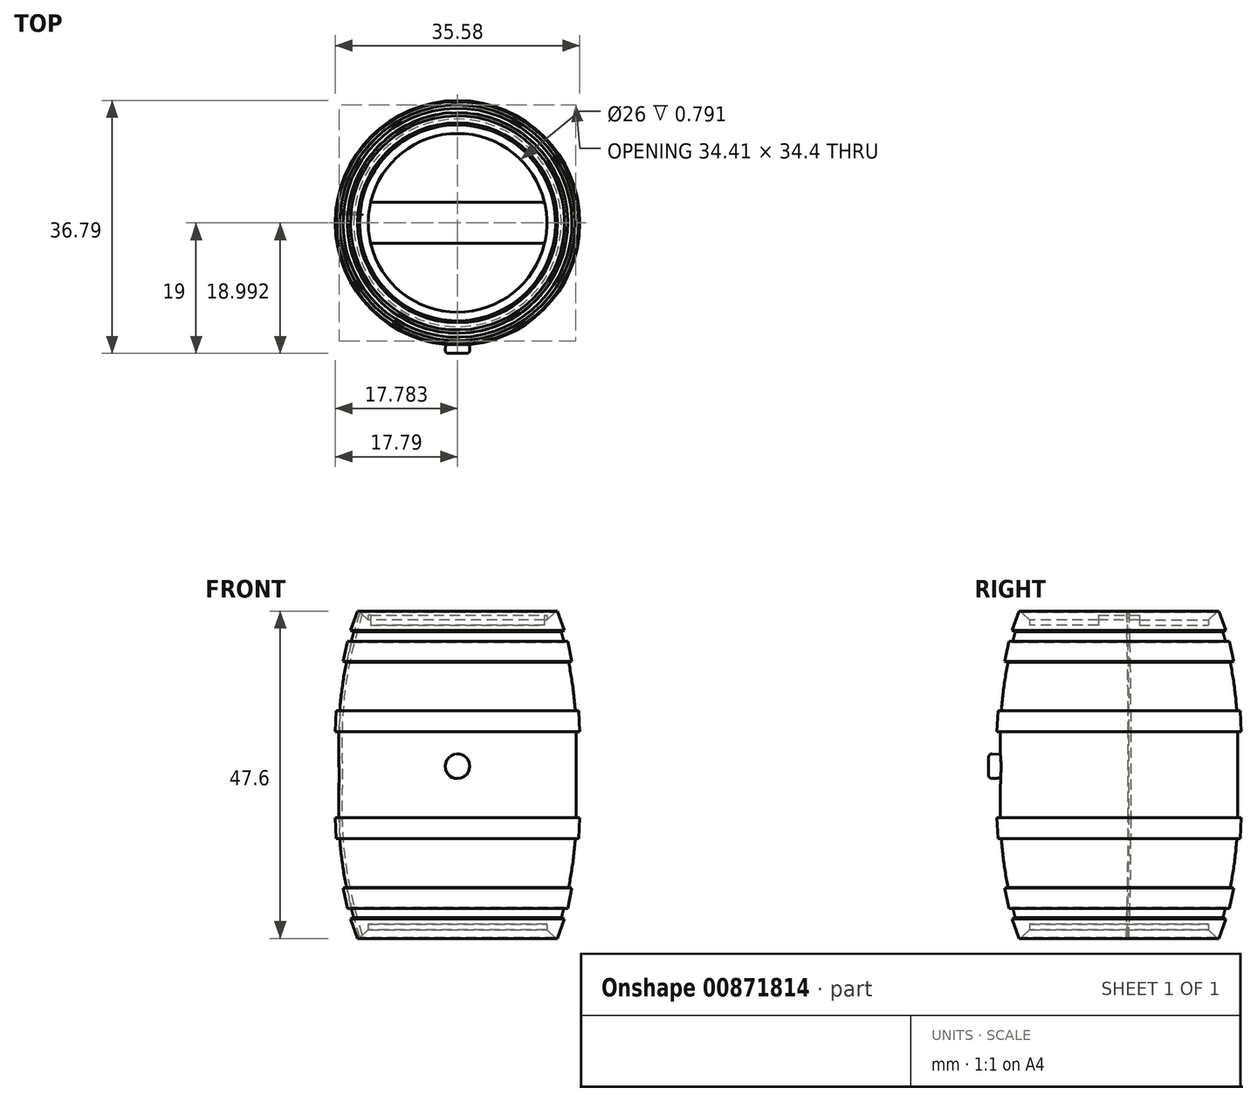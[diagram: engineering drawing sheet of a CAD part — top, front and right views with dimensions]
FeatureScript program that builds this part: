
annotation { "Feature Type Name" : "Feature", "Feature Type Description" : "" }
export const myFeature = defineFeature(function(context is Context, id is Id, definition is map)
    precondition{}
    {
        {
            var Q0;
            Q0=qCreatedBy(makeId("Front.planeOp"),FACE);
            var sketch = newSketch(context, id + "F0", { "sketchPlane" : qUnion([Q0])});
            skLineSegment(sketch, "E0.left", {"start": v(0, 2) * mm, "end": v(0, 45.5) * mm});
            skLineSegment(sketch, "E0.right", {"start": v(-14.25, 0.06) * mm, "end": v(-14.25, 47.44) * mm, "construction": true});
            skPoint(sketch, "E1.positionSnap0", {"position": v(-14.25, 23.75) * mm});
            skFitSpline(sketch, "E2", {"points": [v(-14.25, 0.06) * mm, v(-17.25, 23.75) * mm, v(-14.25, 47.44) * mm], "startDerivative": vector(-21.33, 67.5) * mm, "endDerivative": vector(21.33, 67.5) * mm});
            skLineSegment(sketch, "E3", {"start": v(-13, 45.5) * mm, "end": v(0, 45.5) * mm});
            skLineSegment(sketch, "E4", {"start": v(-13, 45.5) * mm, "end": v(-13, 46.3) * mm});
            skLineSegment(sketch, "E5", {"start": v(-13, 46.3) * mm, "end": v(-14.25, 47.44) * mm});
            skLineSegment(sketch, "E6", {"start": v(6.25, 23.75) * mm, "end": v(9.53, 23.75) * mm, "construction": true});
            skPoint(sketch, "E6.startSnap0", {"position": v(0, 23.75) * mm});
            skLineSegment(sketch, "E7", {"start": v(-14.25, 47.44) * mm, "end": v(-14.55, 47.55) * mm});
            skLineSegment(sketch, "E8", {"start": v(-14.55, 47.55) * mm, "end": v(-15.57, 44.73) * mm});
            skLineSegment(sketch, "E9", {"start": v(-15.57, 44.73) * mm, "end": v(-15.1, 44.56) * mm});
            skLineSegment(sketch, "E10", {"start": v(-15.5, 43.06) * mm, "end": v(-16.03, 43.17) * mm});
            skLineSegment(sketch, "E11", {"start": v(-16.03, 43.17) * mm, "end": v(-16.65, 40.23) * mm});
            skLineSegment(sketch, "E12", {"start": v(-16.65, 40.23) * mm, "end": v(-16.17, 40.13) * mm});
            skPoint(sketch, "E13.orphan", {"position": v(0, 47.5) * mm});
            skLineSegment(sketch, "E14", {"start": v(-17.14, 33) * mm, "end": v(-17.63, 33.04) * mm});
            skLineSegment(sketch, "E15", {"start": v(-17.63, 33.04) * mm, "end": v(-17.8, 30) * mm});
            skLineSegment(sketch, "E16", {"start": v(-17.8, 30) * mm, "end": v(-17.27, 30) * mm});
            skLineSegment(sketch, "E17.MirrorCS", {"start": v(-14.25, 0.06) * mm, "end": v(-14.55, -0.05) * mm});
            skLineSegment(sketch, "E18.MirrorCS", {"start": v(-15.57, 2.77) * mm, "end": v(-15.1, 2.94) * mm});
            skLineSegment(sketch, "E19.MirrorCS", {"start": v(-17.8, 17.5) * mm, "end": v(-17.27, 17.5) * mm});
            skLineSegment(sketch, "E20.MirrorCS", {"start": v(-16.65, 7.27) * mm, "end": v(-16.17, 7.37) * mm});
            skLineSegment(sketch, "E21.MirrorCS", {"start": v(-17.14, 14.5) * mm, "end": v(-17.63, 14.46) * mm});
            skLineSegment(sketch, "E22.MirrorCS", {"start": v(-15.5, 4.44) * mm, "end": v(-16.03, 4.33) * mm});
            skLineSegment(sketch, "E23.MirrorCS", {"start": v(-17.63, 14.46) * mm, "end": v(-17.8, 17.5) * mm});
            skLineSegment(sketch, "E24.MirrorCS", {"start": v(-14.55, -0.05) * mm, "end": v(-15.57, 2.77) * mm});
            skLineSegment(sketch, "E25.MirrorCS", {"start": v(-16.03, 4.33) * mm, "end": v(-16.65, 7.27) * mm});
            skLineSegment(sketch, "E26.MirrorCS", {"start": v(-13, 2) * mm, "end": v(0, 2) * mm});
            skLineSegment(sketch, "E27.MirrorCS", {"start": v(-13, 2) * mm, "end": v(-13, 1.2) * mm});
            skLineSegment(sketch, "E28.MirrorCS", {"start": v(-13, 1.2) * mm, "end": v(-14.25, 0.06) * mm});
            skPoint(sketch, "E29.orphan", {"position": v(0, 0) * mm});
            skSolve(sketch);
        }
        {
            var Q0;
            Q0=makeQuery(id+"F0.imprint","IMPRINT",FACE,{"disambiguationData":[TD([[makeQuery(id+"F0.imprint","IMPRINT",EDGE,{"derivedFrom":sQuery(id+"F0.wireOp",EDGE,"E0.left")}),1.0]])]});
            var Q1;
            Q1=sQuery(id+"F0.wireOp",EDGE,"E0.left");
            revolve(context, id + "F1", {"surfaceOperationType" : NewSurfaceOperationType.NEW, "entities" : qUnion([Q0]), "axis" : qUnion([Q1]), "revolveType" : RevolveType.FULL});
        }
        {
            var Q0;
            Q0=qCreatedBy(makeId("Top.planeOp"),FACE);
            var sketch = newSketch(context, id + "F2", { "sketchPlane" : qUnion([Q0])});
            skLineSegment(sketch, "E30", {"start": v(-13.75, 0) * mm, "end": v(6.9, 0) * mm, "construction": true});
            skLineSegment(sketch, "E31", {"start": v(-14.35, 0.22) * mm, "end": v(-13.75, 0) * mm});
            skLineSegment(sketch, "E32", {"start": v(-14.35, -0.22) * mm, "end": v(-14.35, 0.22) * mm});
            skLineSegment(sketch, "E33", {"start": v(-13.75, 0) * mm, "end": v(-14.35, -0.22) * mm});
            skSolve(sketch);
        }
        {
            var Q0;
            Q0=makeQuery(id+"F2.imprint","IMPRINT",FACE,{"disambiguationData":[TD([[makeQuery(id+"F2.imprint","IMPRINT",EDGE,{"derivedFrom":sQuery(id+"F2.wireOp",EDGE,"E31")}),-1.0]])]});
            var Q1;
            Q1=sQuery(id+"F0.wireOp",EDGE,"E2");
            sweep(context, id + "F3", {"operationType" : NewBodyOperationType.REMOVE, "profiles" : qUnion([Q0]), "path" : qUnion([Q1])});
        }
        {
            var Q0;
            {var subQ0=sQuery(id+"F0.wireOp",EDGE,"E7");Q0=makeQuery(id+"F0.imprint","IMPRINT",FACE,{"disambiguationData":[TD([[makeQuery(id+"F0.imprint","IMPRINT",EDGE,{"derivedFrom":subQ0}),1.0]])]});}
            var Q1;
            {var subQ0=sQuery(id+"F0.wireOp",EDGE,"E10");Q1=makeQuery(id+"F0.imprint","IMPRINT",FACE,{"disambiguationData":[TD([[makeQuery(id+"F0.imprint","IMPRINT",EDGE,{"derivedFrom":subQ0}),1.0]])]});}
            var Q2;
            {var subQ0=sQuery(id+"F0.wireOp",EDGE,"E14");Q2=makeQuery(id+"F0.imprint","IMPRINT",FACE,{"disambiguationData":[TD([[makeQuery(id+"F0.imprint","IMPRINT",EDGE,{"derivedFrom":subQ0}),1.0]])]});}
            var Q3;
            {var subQ0=sQuery(id+"F0.wireOp",EDGE,"E19.MirrorCS");Q3=makeQuery(id+"F0.imprint","IMPRINT",FACE,{"disambiguationData":[TD([[makeQuery(id+"F0.imprint","IMPRINT",EDGE,{"derivedFrom":subQ0}),-1.0]])]});}
            var Q4;
            {var subQ0=sQuery(id+"F0.wireOp",EDGE,"E20.MirrorCS");Q4=makeQuery(id+"F0.imprint","IMPRINT",FACE,{"disambiguationData":[TD([[makeQuery(id+"F0.imprint","IMPRINT",EDGE,{"derivedFrom":subQ0}),-1.0]])]});}
            var Q5;
            {var subQ0=sQuery(id+"F0.wireOp",EDGE,"E17.MirrorCS");Q5=makeQuery(id+"F0.imprint","IMPRINT",FACE,{"disambiguationData":[TD([[makeQuery(id+"F0.imprint","IMPRINT",EDGE,{"derivedFrom":subQ0}),-1.0]])]});}
            var Q6;
            Q6=sQuery(id+"F0.wireOp",EDGE,"E0.left");
            revolve(context, id + "F4", {"operationType" : NewBodyOperationType.ADD, "surfaceOperationType" : NewSurfaceOperationType.NEW, "entities" : qUnion([Q0, Q1, Q2, Q3, Q4, Q5]), "axis" : qUnion([Q6]), "revolveType" : RevolveType.FULL});
        }
        {
            var Q0;
            Q0=makeQuery(id+"F1.opRevolve","SWEPT_BODY",BODY,{"disambiguationData":[OSD([sQuery(id+"F0.wireOp",EDGE,"E0.left"),sQuery(id+"F0.wireOp",EDGE,"E2"),sQuery(id+"F0.wireOp",EDGE,"E3"),sQuery(id+"F0.wireOp",EDGE,"E4"),sQuery(id+"F0.wireOp",EDGE,"E5"),sQuery(id+"F0.wireOp",EDGE,"E26.MirrorCS"),sQuery(id+"F0.wireOp",EDGE,"E27.MirrorCS"),sQuery(id+"F0.wireOp",EDGE,"E28.MirrorCS")])]});
            var Q1;
            Q1=sQuery(id+"F0.wireOp",EDGE,"E0.left");
            var Q2;
            Q2=sQuery(id+"F0.wireOp",EDGE,"E0.left");
            transform(context, id + "F5", {"entities" : qUnion([Q0]), "transformType" : TransformType.ROTATION, "transformAxis" : qUnion([Q2]), "angle" : 5 * degree, "oppositeDirection" : true, "makeCopy" : false});
        }
        {
            var Q0;
            Q0=qCreatedBy(makeId("Front.planeOp"),FACE);
            var sketch = newSketch(context, id + "F6", { "sketchPlane" : qUnion([Q0])});
            skCircle(sketch, "E34", {"center": v(0, 25) * mm, "radius": 0.5 * mm});
            skSolve(sketch);
        }
        {
            var Q0;
            Q0 = qSketchRegion(id + "F6", true);
            extrude(context, id + "F7", {"entities" : qUnion([Q0]), "operationType" : NewBodyOperationType.ADD, "depth" : 19 * mm, "offsetDistance" : 25 * mm, "hasDraft" : true, "draftAngle" : 4 * degree});
        }
        {
            var Q0;
            Q0=makeQuery(id+"F1.opRevolve","SWEPT_FACE",FACE,{"disambiguationData":[OSD([sQuery(id+"F0.wireOp",EDGE,"E3")])]});
            var sketch = newSketch(context, id + "F8", { "sketchPlane" : qUnion([Q0])});
            skLineSegment(sketch, "E35.bottom", {"start": v(-13, -3) * mm, "end": v(13, -3) * mm});
            skLineSegment(sketch, "E35.top", {"start": v(-13, 3) * mm, "end": v(13, 3) * mm});
            skLineSegment(sketch, "E35.left", {"start": v(-13, -3) * mm, "end": v(-13, 3) * mm});
            skLineSegment(sketch, "E35.right", {"start": v(13, -3) * mm, "end": v(13, 3) * mm});
            skLineSegment(sketch, "E36", {"start": v(-20.6, 0) * mm, "end": v(-16.97, 0) * mm, "construction": true});
            skSolve(sketch);
        }
        {
            var Q0;
            {var subQ0=sQuery(id+"F8.wireOp",EDGE,"E35.bottom");var subQ1=makeQuery(id+"F1.opRevolve","SWEPT_EDGE",EDGE,{"disambiguationData":[OSD([sQuery(id+"F0.wireOp",EDGE,"E3"),sQuery(id+"F0.wireOp",EDGE,"E4")])]});var subQ4=makeQuery(id+"F8.imprint","INTERSECT",VERTEX,{"disambiguationData":[OD(0.0)],"derivedFrom":[subQ1,subQ0]});Q0=makeQuery(id+"F8.imprint","IMPRINT",FACE,{"disambiguationData":[TD([[makeQuery(id+"F8.imprint","IMPRINT",EDGE,{"disambiguationData":[TD([[subQ4,-1.0]])],"derivedFrom":subQ0}),1.0]])]});}
            extrude(context, id + "F9", {"entities" : qUnion([Q0]), "operationType" : NewBodyOperationType.ADD, "depth" : 1.5 * mm, "offsetDistance" : 25 * mm});
        }
        {
            var Q0;
            Q0=makeQuery(id+"F7.opExtrude","CAP_EDGE",EDGE,{"disambiguationData":[OSD([sQuery(id+"F6.wireOp",EDGE,"E34")])],"isStart":false});
            fillet(context, id + "F10", {"entities" : qUnion([Q0]), "radius" : .5 * mm, "tangentPropagation" : true, "allowEdgeOverflow" : false});
        }
    });
